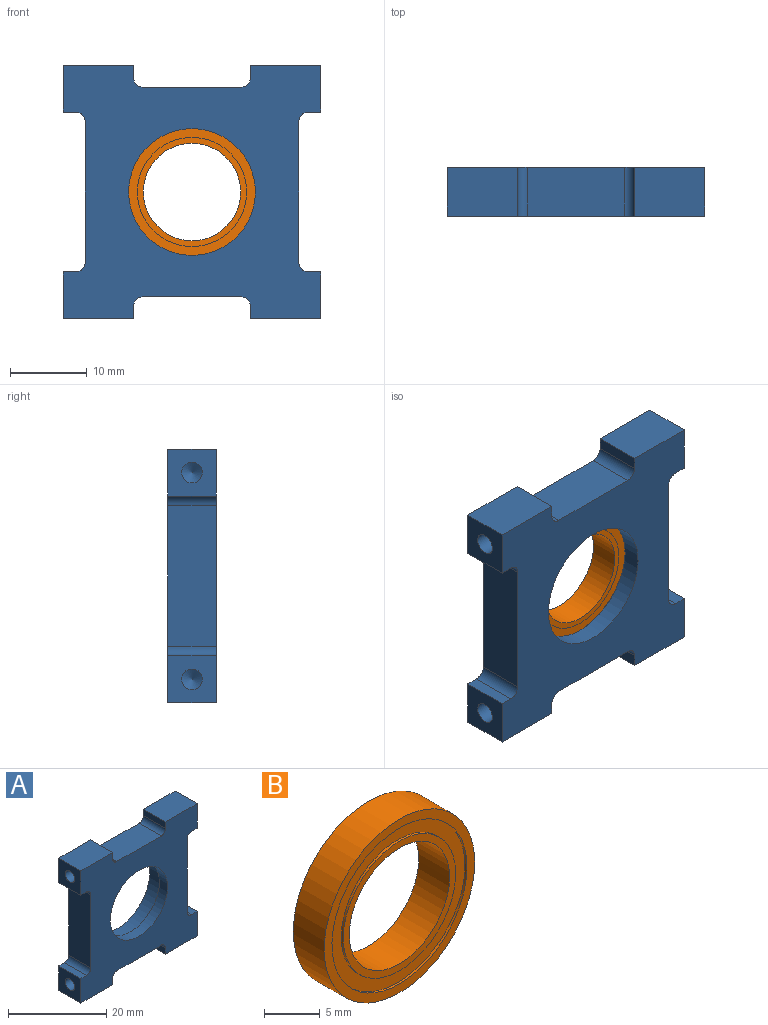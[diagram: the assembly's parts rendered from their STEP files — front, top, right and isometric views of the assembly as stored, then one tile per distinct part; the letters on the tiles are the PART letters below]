
ASSEMBLY  parts=2 mates=1
PART A: 41 faces, bbox 33.5x6.4x33 mm
  f0: cylinder r=8.26mm len=16.51mm, axis (0,1,0), area 123.8mm2, adj f31,f32
  f1: cylinder r=9.53mm len=19.05mm, axis (0,1,0), area 237.1mm2, adj f30,f32
  f2: cylinder r=1.35mm len=7.62mm, axis (1,0,0), area 64.8mm2, adj f3,f26
  f3: cone r=1.35mm half-angle=59deg, axis (1,0,0), area 6.7mm2, adj f2
  f4: cylinder r=1.35mm len=7.62mm, axis (1,0,0), area 64.8mm2, adj f5,f10
  f5: cone r=1.35mm half-angle=59deg, axis (1,0,0), area 6.7mm2, adj f4
  f6: cylinder r=1.35mm len=7.62mm, axis (-1,0,0), area 64.8mm2, adj f7,f20
  f7: cone r=1.35mm half-angle=59deg, axis (-1,0,0), area 6.7mm2, adj f6
  f8: cylinder r=1.35mm len=7.62mm, axis (-1,0,0), area 64.8mm2, adj f9,f16
  f9: cone r=1.35mm half-angle=59deg, axis (-1,0,0), area 6.7mm2, adj f8
  f10: plane 6.35x6.1mm, normal (1,0,0), area 33mm2, adj f4,f11,f29,f30,f31
  f11: plane 9.14x6.35mm, normal (0,0,-1), area 58.1mm2, adj f10,f12,f30,f31
  f12: plane 6.35x1.6mm, normal (-1,0,0), area 10.1mm2, adj f11,f30,f31,f39
  f13: plane 12.7x6.35mm, normal (0,0,-1), area 80.6mm2, adj f30,f31,f38,f39
  f14: plane 6.35x1.6mm, normal (1,0,0), area 10.1mm2, adj f15,f30,f31,f38
  f15: plane 9.14x6.35mm, normal (0,0,-1), area 58.1mm2, adj f14,f16,f30,f31
  f16: plane 6.35x6.1mm, normal (-1,0,0), area 33mm2, adj f8,f15,f17,f30,f31
  f17: plane 6.35x1.59mm, normal (0,0,1), area 10.1mm2, adj f16,f30,f31,f40
  f18: plane 18.29x6.35mm, normal (-1,0,0), area 116.1mm2, adj f30,f31,f37,f40
  f19: plane 6.35x1.59mm, normal (0,0,-1), area 10.1mm2, adj f20,f30,f31,f37
  f20: plane 6.35x6.1mm, normal (-1,0,0), area 33mm2, adj f6,f19,f21,f30,f31
  f21: plane 9.14x6.35mm, normal (0,0,1), area 58.1mm2, adj f20,f22,f30,f31
  f22: plane 6.35x1.6mm, normal (1,0,0), area 10.1mm2, adj f21,f30,f31,f36
  f23: plane 12.7x6.35mm, normal (0,0,1), area 80.6mm2, adj f30,f31,f35,f36
  f24: plane 6.35x1.6mm, normal (-1,0,0), area 10.1mm2, adj f25,f30,f31,f35
  f25: plane 9.14x6.35mm, normal (0,0,1), area 58.1mm2, adj f24,f26,f30,f31
  f26: plane 6.35x6.1mm, normal (1,0,0), area 33mm2, adj f2,f25,f27,f30,f31
  f27: plane 6.35x1.59mm, normal (0,0,-1), area 10.1mm2, adj f26,f30,f31,f34
  f28: plane 18.29x6.35mm, normal (1,0,0), area 116.1mm2, adj f30,f31,f33,f34
  f29: plane 6.35x1.59mm, normal (0,0,1), area 10.1mm2, adj f10,f30,f31,f33
  f30: plane 33.53x33.02mm, normal (0,1,0), area 618.5mm2, adj f1,f10,f11,f12,f13,f14,f15,f16
  f31: plane 33.53x33.02mm, normal (0,-1,0), area 689.4mm2, adj f0,f10,f11,f12,f13,f14,f15,f16
  f32: plane 19.05x19.05mm, normal (0,1,0), area 70.9mm2, adj f0,f1
  f33: cylinder r=1.27mm len=6.35mm, axis (0,1,0), area 12.7mm2, adj f28,f29,f30,f31
  f34: cylinder r=1.27mm len=6.35mm, axis (0,1,0), area 12.7mm2, adj f27,f28,f30,f31
  f35: cylinder r=1.27mm len=6.35mm, axis (0,1,0), area 12.7mm2, adj f23,f24,f30,f31
  f36: cylinder r=1.27mm len=6.35mm, axis (0,1,0), area 12.7mm2, adj f22,f23,f30,f31
  f37: cylinder r=1.27mm len=6.35mm, axis (0,1,0), area 12.7mm2, adj f18,f19,f30,f31
  f38: cylinder r=1.27mm len=6.35mm, axis (0,1,0), area 12.7mm2, adj f13,f14,f30,f31
  f39: cylinder r=1.27mm len=6.35mm, axis (0,1,0), area 12.7mm2, adj f12,f13,f30,f31
  f40: cylinder r=1.27mm len=6.35mm, axis (0,1,0), area 12.7mm2, adj f17,f18,f30,f31
PART B: 12 faces, bbox 19.1x3.9x19.1 mm
  f0: cylinder r=7.11mm len=14.22mm, axis (0,-1,0), area 11.4mm2, adj f6,f11
  f1: cylinder r=8.55mm len=17.09mm, axis (0,-1,0), area 13.6mm2, adj f9,f11
  f2: cylinder r=7.11mm len=14.22mm, axis (0,1,0), area 11.4mm2, adj f7,f10
  f3: cylinder r=8.55mm len=17.09mm, axis (0,1,0), area 13.6mm2, adj f8,f10
  f4: cylinder r=6.35mm len=12.7mm, axis (0,-1,0), area 156.1mm2, adj f6,f7
  f5: cylinder r=9.53mm len=19.05mm, axis (0,-1,0), area 234.1mm2, adj f8,f9
  f6: plane 14.22x14.22mm, normal (0,-1,0), area 32.2mm2, adj f0,f4
  f7: plane 14.22x14.22mm, normal (0,1,0), area 32.2mm2, adj f2,f4
  f8: plane 19.05x19.05mm, normal (0,1,0), area 55.5mm2, adj f3,f5
  f9: plane 19.05x19.05mm, normal (0,-1,0), area 55.5mm2, adj f1,f5
  f10: plane 17.09x17.09mm, normal (0,1,0), area 70.6mm2, adj f2,f3
  f11: plane 17.09x17.09mm, normal (0,-1,0), area 70.6mm2, adj f0,f1
PLACE A t=(8.36,13.24,28.67)mm
PLACE B t=(8.36,15.63,28.67)mm
MATE fastened B.f0 <-> A.f0  axis (0,-1,0) through (8.36,15.88,28.67)mm
